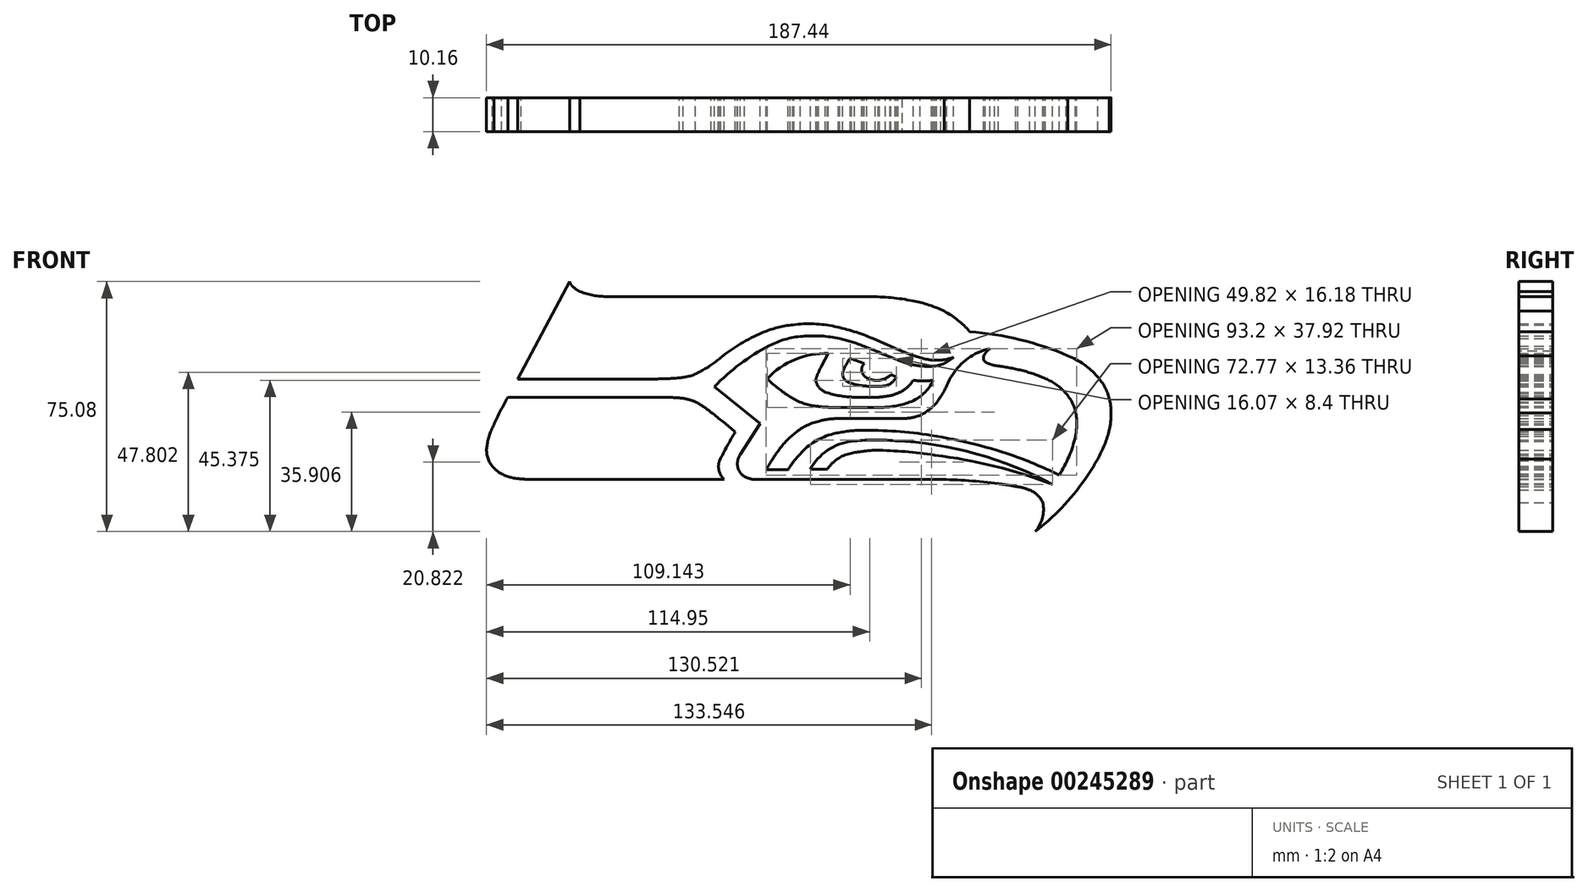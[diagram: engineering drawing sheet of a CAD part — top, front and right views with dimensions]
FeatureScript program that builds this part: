
annotation { "Feature Type Name" : "Feature", "Feature Type Description" : "" }
export const myFeature = defineFeature(function(context is Context, id is Id, definition is map)
    precondition{}
    {
        {
            var Q0;
            Q0=qCreatedBy(makeId("Front.planeOp"),FACE);
            var sketch = newSketch(context, id + "F0", { "sketchPlane" : qUnion([Q0])});
            skPoint(sketch, "E0", {"position": v(83.1, -14.56) * mm});
            skPoint(sketch, "E1", {"position": v(53.3, 23.61) * mm});
            skPoint(sketch, "E2", {"position": v(-2.59, 17.22) * mm});
            skPoint(sketch, "E3", {"position": v(-18.44, 14.8) * mm});
            skLineSegment(sketch, "E4", {"start": v(-77.5, 17.11) * mm, "end": v(-61.9, 46.38) * mm});
            skPoint(sketch, "E5", {"position": v(-77.5, 17.11) * mm});
            skLineSegment(sketch, "E6", {"start": v(-80.45, 11.57) * mm, "end": v(-32.35, 11.57) * mm});
            skLineSegment(sketch, "E7", {"start": v(-77.5, 17.11) * mm, "end": v(-36.51, 17.11) * mm});
            skPoint(sketch, "E8", {"position": v(-4.71, 3.77) * mm});
            skPoint(sketch, "E9", {"position": v(-12.17, 1.23) * mm});
            skLineSegment(sketch, "E10", {"start": v(-18.44, 14.8) * mm, "end": v(-4.71, 3.77) * mm});
            skPoint(sketch, "E11", {"position": v(48.88, -13.09) * mm});
            skPoint(sketch, "E12", {"position": v(3.66, -13.09) * mm});
            skLineSegment(sketch, "E13", {"start": v(3.66, -13.09) * mm, "end": v(48.88, -13.09) * mm});
            skPoint(sketch, "E14", {"position": v(27.95, 41.83) * mm});
            skPoint(sketch, "E15", {"position": v(-50.49, 41.83) * mm});
            skLineSegment(sketch, "E16", {"start": v(-50.49, 41.83) * mm, "end": v(27.95, 41.83) * mm});
            skPoint(sketch, "E17", {"position": v(-15.51, -13.08) * mm});
            skPoint(sketch, "E18", {"position": v(-72.6, -13.08) * mm});
            skLineSegment(sketch, "E19", {"start": v(-72.6, -13.08) * mm, "end": v(-15.51, -13.08) * mm});
            skArc(sketch, "E20", {"start": v(-80.45, 11.57) * mm, "mid": v(-82.64, 7.5) * mm, "end": v(-84.65, 3.32) * mm});
            skArc(sketch, "E21", {"start": v(-84.65, 3.32) * mm, "mid": v(-85.98, 0.1) * mm, "end": v(-86.75, -3.29) * mm});
            skArc(sketch, "E22", {"start": v(-86.75, -3.29) * mm, "mid": v(-86.53, -6.36) * mm, "end": v(-85.07, -9.07) * mm});
            skArc(sketch, "E23", {"start": v(-85.07, -9.07) * mm, "mid": v(-83.8, -10.4) * mm, "end": v(-82.26, -11.42) * mm});
            skArc(sketch, "E24", {"start": v(-82.26, -11.42) * mm, "mid": v(-79.46, -12.44) * mm, "end": v(-76.5, -12.87) * mm});
            skArc(sketch, "E25", {"start": v(-76.5, -12.87) * mm, "mid": v(-74.55, -13.03) * mm, "end": v(-72.6, -13.08) * mm});
            skArc(sketch, "E26", {"start": v(-17.23, -9.28) * mm, "mid": v(-16.72, -11.33) * mm, "end": v(-15.51, -13.08) * mm});
            skArc(sketch, "E27", {"start": v(-16.87, -7.42) * mm, "mid": v(-17.14, -8.33) * mm, "end": v(-17.23, -9.28) * mm});
            skArc(sketch, "E28", {"start": v(-12.17, 1.23) * mm, "mid": v(-14.63, -3.04) * mm, "end": v(-16.87, -7.42) * mm});
            skArc(sketch, "E29", {"start": v(-12.17, 1.23) * mm, "mid": v(-15.75, 4.2) * mm, "end": v(-19.4, 7.08) * mm});
            skArc(sketch, "E30", {"start": v(-19.4, 7.08) * mm, "mid": v(-21.67, 8.77) * mm, "end": v(-24.1, 10.24) * mm});
            skArc(sketch, "E31", {"start": v(-24.1, 10.24) * mm, "mid": v(-25.94, 10.88) * mm, "end": v(-27.86, 11.3) * mm});
            skArc(sketch, "E32", {"start": v(-27.86, 11.3) * mm, "mid": v(-30.1, 11.5) * mm, "end": v(-32.35, 11.57) * mm});
            skArc(sketch, "E33", {"start": v(-61.9, 46.38) * mm, "mid": v(-61.6, 45.72) * mm, "end": v(-61.17, 45.13) * mm});
            skArc(sketch, "E34", {"start": v(-61.17, 45.13) * mm, "mid": v(-60.08, 44.13) * mm, "end": v(-58.82, 43.35) * mm});
            skArc(sketch, "E35", {"start": v(-58.82, 43.35) * mm, "mid": v(-54.73, 42.22) * mm, "end": v(-50.49, 41.83) * mm});
            skPoint(sketch, "E36", {"position": v(15.73, 24.77) * mm});
            skPoint(sketch, "E37", {"position": v(22.28, 23.3) * mm});
            skArc(sketch, "E38", {"start": v(-36.51, 17.11) * mm, "mid": v(-32.76, 17.2) * mm, "end": v(-29.02, 17.45) * mm});
            skArc(sketch, "E39", {"start": v(-29.02, 17.45) * mm, "mid": v(-25.84, 18) * mm, "end": v(-22.84, 19.23) * mm});
            skArc(sketch, "E40", {"start": v(-22.84, 19.23) * mm, "mid": v(-19.58, 21.2) * mm, "end": v(-16.56, 23.52) * mm});
            skArc(sketch, "E41", {"start": v(-4.04, 31.03) * mm, "mid": v(-10.55, 27.69) * mm, "end": v(-16.56, 23.52) * mm});
            skArc(sketch, "E42", {"start": v(5.12, 33.37) * mm, "mid": v(0.45, 32.54) * mm, "end": v(-4.04, 31.03) * mm});
            skArc(sketch, "E43", {"start": v(17.75, 32.87) * mm, "mid": v(11.46, 33.66) * mm, "end": v(5.12, 33.37) * mm});
            skArc(sketch, "E44", {"start": v(29.14, 29.25) * mm, "mid": v(23.53, 31.33) * mm, "end": v(17.75, 32.87) * mm});
            skArc(sketch, "E45", {"start": v(29.14, 29.25) * mm, "mid": v(33.48, 27.38) * mm, "end": v(37.82, 25.5) * mm});
            skArc(sketch, "E46", {"start": v(37.82, 25.5) * mm, "mid": v(41.16, 24.17) * mm, "end": v(44.62, 23.16) * mm});
            skArc(sketch, "E47", {"start": v(44.62, 23.16) * mm, "mid": v(47.08, 22.77) * mm, "end": v(49.56, 22.76) * mm});
            skArc(sketch, "E48", {"start": v(49.56, 22.76) * mm, "mid": v(51.46, 23.05) * mm, "end": v(53.3, 23.61) * mm});
            skPoint(sketch, "E49", {"position": v(58.16, 31.3) * mm});
            skArc(sketch, "E50", {"start": v(46.67, 20.92) * mm, "mid": v(50.24, 21.64) * mm, "end": v(53.3, 23.61) * mm});
            skArc(sketch, "E51", {"start": v(42.4, 21.15) * mm, "mid": v(44.53, 20.93) * mm, "end": v(46.67, 20.92) * mm});
            skArc(sketch, "E52", {"start": v(36.65, 22.8) * mm, "mid": v(39.47, 21.8) * mm, "end": v(42.4, 21.15) * mm});
            skArc(sketch, "E53", {"start": v(36.65, 22.8) * mm, "mid": v(31.5, 24.87) * mm, "end": v(26.36, 26.94) * mm});
            skArc(sketch, "E54", {"start": v(26.36, 26.94) * mm, "mid": v(22.83, 28.25) * mm, "end": v(19.2, 29.25) * mm});
            skArc(sketch, "E55", {"start": v(19.2, 29.25) * mm, "mid": v(13.6, 30) * mm, "end": v(7.95, 29.93) * mm});
            skArc(sketch, "E56", {"start": v(7.95, 29.93) * mm, "mid": v(2.8, 29) * mm, "end": v(-2.05, 27.06) * mm});
            skArc(sketch, "E57", {"start": v(-2.05, 27.06) * mm, "mid": v(-10.74, 21.59) * mm, "end": v(-18.44, 14.8) * mm});
            skPoint(sketch, "E58", {"position": v(-4.1, -13.09) * mm});
            skLineSegment(sketch, "E59", {"start": v(-4.1, -13.09) * mm, "end": v(3.66, -13.09) * mm});
            skLineSegment(sketch, "E60", {"start": v(-4.1, -13.09) * mm, "end": v(-5.96, -13.09) * mm});
            skArc(sketch, "E61", {"start": v(-9.44, -12.15) * mm, "mid": v(-7.76, -12.85) * mm, "end": v(-5.96, -13.09) * mm});
            skArc(sketch, "E62", {"start": v(-11.4, -9.51) * mm, "mid": v(-10.66, -11) * mm, "end": v(-9.44, -12.15) * mm});
            skArc(sketch, "E63", {"start": v(-10.74, -5.6) * mm, "mid": v(-11.44, -7.5) * mm, "end": v(-11.4, -9.51) * mm});
            skLineSegment(sketch, "E64", {"start": v(-4.71, 3.77) * mm, "end": v(-10.74, -5.6) * mm});
            skPoint(sketch, "E65", {"position": v(77.83, -28.7) * mm});
            skArc(sketch, "E66", {"start": v(41.18, 40.57) * mm, "mid": v(34.6, 41.52) * mm, "end": v(27.95, 41.83) * mm});
            skArc(sketch, "E67", {"start": v(50.53, 37.46) * mm, "mid": v(45.95, 39.31) * mm, "end": v(41.18, 40.57) * mm});
            skArc(sketch, "E68", {"start": v(58.16, 31.3) * mm, "mid": v(54.66, 34.77) * mm, "end": v(50.53, 37.46) * mm});
            skArc(sketch, "E69", {"start": v(87.67, 24.07) * mm, "mid": v(73.22, 28.92) * mm, "end": v(58.16, 31.3) * mm});
            skArc(sketch, "E70", {"start": v(96.52, 17.84) * mm, "mid": v(92.46, 21.47) * mm, "end": v(87.67, 24.07) * mm});
            skArc(sketch, "E71", {"start": v(100.12, 11.11) * mm, "mid": v(98.73, 14.7) * mm, "end": v(96.52, 17.84) * mm});
            skArc(sketch, "E72", {"start": v(100.61, 6.88) * mm, "mid": v(100.5, 9) * mm, "end": v(100.12, 11.11) * mm});
            skArc(sketch, "E73", {"start": v(100.12, 1.89) * mm, "mid": v(100.5, 4.37) * mm, "end": v(100.61, 6.88) * mm});
            skArc(sketch, "E74", {"start": v(96.6, -6.91) * mm, "mid": v(98.68, -2.64) * mm, "end": v(100.12, 1.89) * mm});
            skArc(sketch, "E75", {"start": v(92.65, -13.2) * mm, "mid": v(94.72, -10.1) * mm, "end": v(96.6, -6.91) * mm});
            skArc(sketch, "E76", {"start": v(77.83, -28.7) * mm, "mid": v(85.84, -21.52) * mm, "end": v(92.65, -13.2) * mm});
            skArc(sketch, "E77", {"start": v(66.8, -14.37) * mm, "mid": v(57.86, -13.4) * mm, "end": v(48.88, -13.09) * mm});
            skArc(sketch, "E78", {"start": v(72, -15.16) * mm, "mid": v(69.4, -14.7) * mm, "end": v(66.8, -14.37) * mm});
            skArc(sketch, "E79", {"start": v(76.2, -16.26) * mm, "mid": v(74.13, -15.57) * mm, "end": v(72, -15.16) * mm});
            skArc(sketch, "E80", {"start": v(80.12, -20.01) * mm, "mid": v(78.54, -17.74) * mm, "end": v(76.2, -16.26) * mm});
            skArc(sketch, "E81", {"start": v(77.83, -28.7) * mm, "mid": v(80, -24.62) * mm, "end": v(80.12, -20.01) * mm});
            skArc(sketch, "E82", {"start": v(15.73, 24.77) * mm, "mid": v(5.76, 22.96) * mm, "end": v(-2.59, 17.22) * mm});
            skLineSegment(sketch, "E83", {"start": v(15.73, 24.77) * mm, "end": v(13.68, 20.97) * mm});
            skArc(sketch, "E84", {"start": v(-2.59, 17.22) * mm, "mid": v(0.74, 14.29) * mm, "end": v(4.36, 11.73) * mm});
            skArc(sketch, "E85", {"start": v(4.36, 11.73) * mm, "mid": v(8.03, 9.89) * mm, "end": v(12.04, 8.96) * mm});
            skLineSegment(sketch, "E86", {"start": v(17.17, 8.58) * mm, "end": v(31.1, 8.58) * mm});
            skArc(sketch, "E87", {"start": v(12.04, 8.96) * mm, "mid": v(14.6, 8.68) * mm, "end": v(17.17, 8.58) * mm});
            skPoint(sketch, "E88", {"position": v(47.23, 16.72) * mm});
            skPoint(sketch, "E89", {"position": v(41.25, 16.75) * mm});
            skArc(sketch, "E90", {"start": v(41.25, 16.75) * mm, "mid": v(44.24, 16.5) * mm, "end": v(47.23, 16.72) * mm});
            skArc(sketch, "E91", {"start": v(31.1, 8.58) * mm, "mid": v(35.69, 8.98) * mm, "end": v(40.14, 10.15) * mm});
            skArc(sketch, "E92", {"start": v(40.14, 10.15) * mm, "mid": v(44.37, 12.7) * mm, "end": v(47.23, 16.72) * mm});
            skArc(sketch, "E93", {"start": v(37.97, 13.54) * mm, "mid": v(39.82, 14.94) * mm, "end": v(41.25, 16.75) * mm});
            skArc(sketch, "E94", {"start": v(34.3, 12.11) * mm, "mid": v(36.2, 12.68) * mm, "end": v(37.97, 13.54) * mm});
            skArc(sketch, "E95", {"start": v(30.78, 11.64) * mm, "mid": v(32.55, 11.82) * mm, "end": v(34.3, 12.11) * mm});
            skArc(sketch, "E96", {"start": v(23.67, 11.64) * mm, "mid": v(27.23, 11.54) * mm, "end": v(30.78, 11.64) * mm});
            skArc(sketch, "E97", {"start": v(14.87, 13.15) * mm, "mid": v(19.21, 12.06) * mm, "end": v(23.67, 11.64) * mm});
            skArc(sketch, "E98", {"start": v(12.29, 15.66) * mm, "mid": v(13.34, 14.16) * mm, "end": v(14.87, 13.15) * mm});
            skArc(sketch, "E99", {"start": v(12.36, 17.99) * mm, "mid": v(12.07, 16.83) * mm, "end": v(12.29, 15.66) * mm});
            skArc(sketch, "E100", {"start": v(13.68, 20.97) * mm, "mid": v(12.96, 19.5) * mm, "end": v(12.36, 17.99) * mm});
            skLineSegment(sketch, "E101", {"start": v(22.28, 23.3) * mm, "end": v(26.52, 21.7) * mm});
            skArc(sketch, "E102", {"start": v(22.28, 23.3) * mm, "mid": v(21.3, 21.75) * mm, "end": v(20.45, 20.12) * mm});
            skArc(sketch, "E103", {"start": v(20.45, 20.12) * mm, "mid": v(20.15, 19.16) * mm, "end": v(20.1, 18.16) * mm});
            skArc(sketch, "E104", {"start": v(20.1, 18.16) * mm, "mid": v(20.54, 17.1) * mm, "end": v(21.42, 16.35) * mm});
            skLineSegment(sketch, "E105", {"start": v(28.8, 14.9) * mm, "end": v(30.76, 14.9) * mm});
            skPoint(sketch, "E106", {"position": v(26.35, 15.05) * mm});
            skPoint(sketch, "E107", {"position": v(21.42, 16.35) * mm});
            skArc(sketch, "E108", {"start": v(21.42, 16.35) * mm, "mid": v(23.82, 15.45) * mm, "end": v(26.35, 15.05) * mm});
            skArc(sketch, "E109", {"start": v(26.35, 15.05) * mm, "mid": v(27.57, 14.94) * mm, "end": v(28.8, 14.9) * mm});
            skPoint(sketch, "E110", {"position": v(36.17, 17.74) * mm});
            skArc(sketch, "E111", {"start": v(30.76, 14.9) * mm, "mid": v(31.83, 14.95) * mm, "end": v(32.9, 15.08) * mm});
            skArc(sketch, "E112", {"start": v(32.9, 15.08) * mm, "mid": v(34.83, 16.04) * mm, "end": v(36.17, 17.74) * mm});
            skPoint(sketch, "E113", {"position": v(34.56, 18.42) * mm});
            skLineSegment(sketch, "E114", {"start": v(36.17, 17.74) * mm, "end": v(34.56, 18.42) * mm});
            skArc(sketch, "E115", {"start": v(26.52, 21.7) * mm, "mid": v(26, 20.99) * mm, "end": v(25.76, 20.13) * mm});
            skArc(sketch, "E116", {"start": v(25.76, 20.13) * mm, "mid": v(25.84, 19.24) * mm, "end": v(26.24, 18.43) * mm});
            skPoint(sketch, "E117", {"position": v(27.28, 17.44) * mm});
            skArc(sketch, "E118", {"start": v(26.24, 18.43) * mm, "mid": v(26.7, 17.88) * mm, "end": v(27.28, 17.44) * mm});
            skPoint(sketch, "E119", {"position": v(31.08, 16.73) * mm});
            skArc(sketch, "E120", {"start": v(27.28, 17.44) * mm, "mid": v(29.13, 16.8) * mm, "end": v(31.08, 16.73) * mm});
            skArc(sketch, "E121", {"start": v(31.08, 16.73) * mm, "mid": v(32.95, 17.3) * mm, "end": v(34.56, 18.42) * mm});
            skLineSegment(sketch, "E122", {"start": v(-2.77, -10.1) * mm, "end": v(3.72, -10.1) * mm});
            skLineSegment(sketch, "E123", {"start": v(-2.77, -10.1) * mm, "end": v(-2.9, -10.1) * mm});
            skPoint(sketch, "E124", {"position": v(0.3, -5.03) * mm});
            skArc(sketch, "E125", {"start": v(0.3, -5.03) * mm, "mid": v(-1.36, -7.52) * mm, "end": v(-2.9, -10.1) * mm});
            skArc(sketch, "E126", {"start": v(5.39, 0.57) * mm, "mid": v(2.65, -2.06) * mm, "end": v(0.3, -5.03) * mm});
            skArc(sketch, "E127", {"start": v(12.79, 4.41) * mm, "mid": v(8.86, 2.93) * mm, "end": v(5.39, 0.57) * mm});
            skArc(sketch, "E128", {"start": v(18.73, 5.24) * mm, "mid": v(15.73, 5.01) * mm, "end": v(12.79, 4.41) * mm});
            skLineSegment(sketch, "E129", {"start": v(18.73, 5.24) * mm, "end": v(37.98, 5.24) * mm});
            skArc(sketch, "E130", {"start": v(37.98, 5.24) * mm, "mid": v(40.65, 5.47) * mm, "end": v(43.24, 6.17) * mm});
            skArc(sketch, "E131", {"start": v(43.24, 6.17) * mm, "mid": v(45.94, 7.84) * mm, "end": v(48.26, 10) * mm});
            skArc(sketch, "E132", {"start": v(48.26, 10) * mm, "mid": v(49.92, 12.5) * mm, "end": v(51.34, 15.16) * mm});
            skArc(sketch, "E133", {"start": v(60.64, 25) * mm, "mid": v(55.05, 20.97) * mm, "end": v(51.34, 15.16) * mm});
            skPoint(sketch, "E134", {"position": v(64.26, 26.17) * mm});
            skArc(sketch, "E135", {"start": v(64.26, 26.17) * mm, "mid": v(62.4, 25.71) * mm, "end": v(60.64, 25) * mm});
            skArc(sketch, "E136", {"start": v(64.26, 26.17) * mm, "mid": v(63.54, 25.6) * mm, "end": v(62.93, 24.92) * mm});
            skPoint(sketch, "E137", {"position": v(65.71, 21.3) * mm});
            skPoint(sketch, "E138", {"position": v(65.71, 21.23) * mm});
            skArc(sketch, "E139", {"start": v(62.93, 24.92) * mm, "mid": v(62.7, 24.55) * mm, "end": v(62.49, 24.16) * mm});
            skPoint(sketch, "E140", {"position": v(65.7, 21.16) * mm});
            skArc(sketch, "E141", {"start": v(62.49, 24.16) * mm, "mid": v(62.33, 23.71) * mm, "end": v(62.3, 23.24) * mm});
            skArc(sketch, "E142", {"start": v(62.3, 23.24) * mm, "mid": v(62.45, 22.68) * mm, "end": v(62.87, 22.27) * mm});
            skArc(sketch, "E143", {"start": v(62.87, 22.27) * mm, "mid": v(64.23, 21.58) * mm, "end": v(65.7, 21.16) * mm});
            skArc(sketch, "E144", {"start": v(73.3, 19.8) * mm, "mid": v(69.52, 20.57) * mm, "end": v(65.7, 21.16) * mm});
            skArc(sketch, "E145", {"start": v(80.92, 17.2) * mm, "mid": v(77.17, 18.69) * mm, "end": v(73.3, 19.8) * mm});
            skArc(sketch, "E146", {"start": v(87.1, 12.73) * mm, "mid": v(84.27, 15.32) * mm, "end": v(80.92, 17.2) * mm});
            skArc(sketch, "E147", {"start": v(90.25, 5.38) * mm, "mid": v(89.29, 9.32) * mm, "end": v(87.1, 12.73) * mm});
            skArc(sketch, "E148", {"start": v(89.94, -0.1) * mm, "mid": v(90.27, 2.63) * mm, "end": v(90.25, 5.38) * mm});
            skArc(sketch, "E149", {"start": v(85.04, -11.76) * mm, "mid": v(88, -6.15) * mm, "end": v(89.94, -0.1) * mm});
            skArc(sketch, "E150", {"start": v(85.04, -11.76) * mm, "mid": v(78.9, -8.92) * mm, "end": v(72.62, -6.41) * mm});
            skPoint(sketch, "E151", {"position": v(46.62, 0.2) * mm});
            skArc(sketch, "E152", {"start": v(72.62, -6.41) * mm, "mid": v(59.77, -2.5) * mm, "end": v(46.62, 0.2) * mm});
            skArc(sketch, "E153", {"start": v(46.62, 0.2) * mm, "mid": v(36.07, 1.4) * mm, "end": v(25.45, 1.7) * mm});
            skArc(sketch, "E154", {"start": v(25.45, 1.7) * mm, "mid": v(21.35, 1.39) * mm, "end": v(17.3, 0.64) * mm});
            skArc(sketch, "E155", {"start": v(17.3, 0.64) * mm, "mid": v(11.85, -1.61) * mm, "end": v(7.33, -5.4) * mm});
            skArc(sketch, "E156", {"start": v(7.33, -5.4) * mm, "mid": v(5.37, -7.63) * mm, "end": v(3.72, -10.1) * mm});
            skArc(sketch, "E157", {"start": v(35.8, -1.44) * mm, "mid": v(29.24, -1.2) * mm, "end": v(22.69, -1.62) * mm});
            skArc(sketch, "E158", {"start": v(22.69, -1.62) * mm, "mid": v(15.53, -4.32) * mm, "end": v(10.34, -9.93) * mm});
            skLineSegment(sketch, "E159", {"start": v(10.34, -9.93) * mm, "end": v(15.46, -9.93) * mm});
            skArc(sketch, "E160", {"start": v(22.36, -5.23) * mm, "mid": v(18.46, -6.92) * mm, "end": v(15.46, -9.93) * mm});
            skArc(sketch, "E161", {"start": v(83.1, -14.56) * mm, "mid": v(65.67, -9.1) * mm, "end": v(47.7, -5.74) * mm});
            skArc(sketch, "E162", {"start": v(47.7, -5.74) * mm, "mid": v(38.8, -4.7) * mm, "end": v(29.86, -4.3) * mm});
            skArc(sketch, "E163", {"start": v(29.86, -4.3) * mm, "mid": v(26.1, -4.6) * mm, "end": v(22.36, -5.23) * mm});
            skArc(sketch, "E164", {"start": v(83.1, -14.56) * mm, "mid": v(60.19, -5.37) * mm, "end": v(35.8, -1.44) * mm});
            skLineSegment(sketch, "E165", {"start": v(26.52, 21.7) * mm, "end": v(34.56, 18.42) * mm});
            skSolve(sketch);
        }
        {
            var Q0;
            Q0=makeQuery(id+"F0.imprint","IMPRINT",FACE,{"disambiguationData":[TD([[makeQuery(id+"F0.imprint","IMPRINT",EDGE,{"derivedFrom":sQuery(id+"F0.wireOp",EDGE,"E4")}),-1.0]])]});
            var Q1;
            Q1=makeQuery(id+"F0.imprint","IMPRINT",FACE,{"disambiguationData":[TD([[makeQuery(id+"F0.imprint","IMPRINT",EDGE,{"derivedFrom":sQuery(id+"F0.wireOp",EDGE,"E6")}),-1.0]])]});
            var Q2;
            Q2=makeQuery(id+"F0.imprint","IMPRINT",FACE,{"disambiguationData":[TD([[makeQuery(id+"F0.imprint","IMPRINT",EDGE,{"derivedFrom":sQuery(id+"F0.wireOp",EDGE,"E115")}),1.0]])]});
            extrude(context, id + "F1", {"entities" : qUnion([Q0, Q1, Q2]), "depth" : 10.16 * mm});
        }
    });
